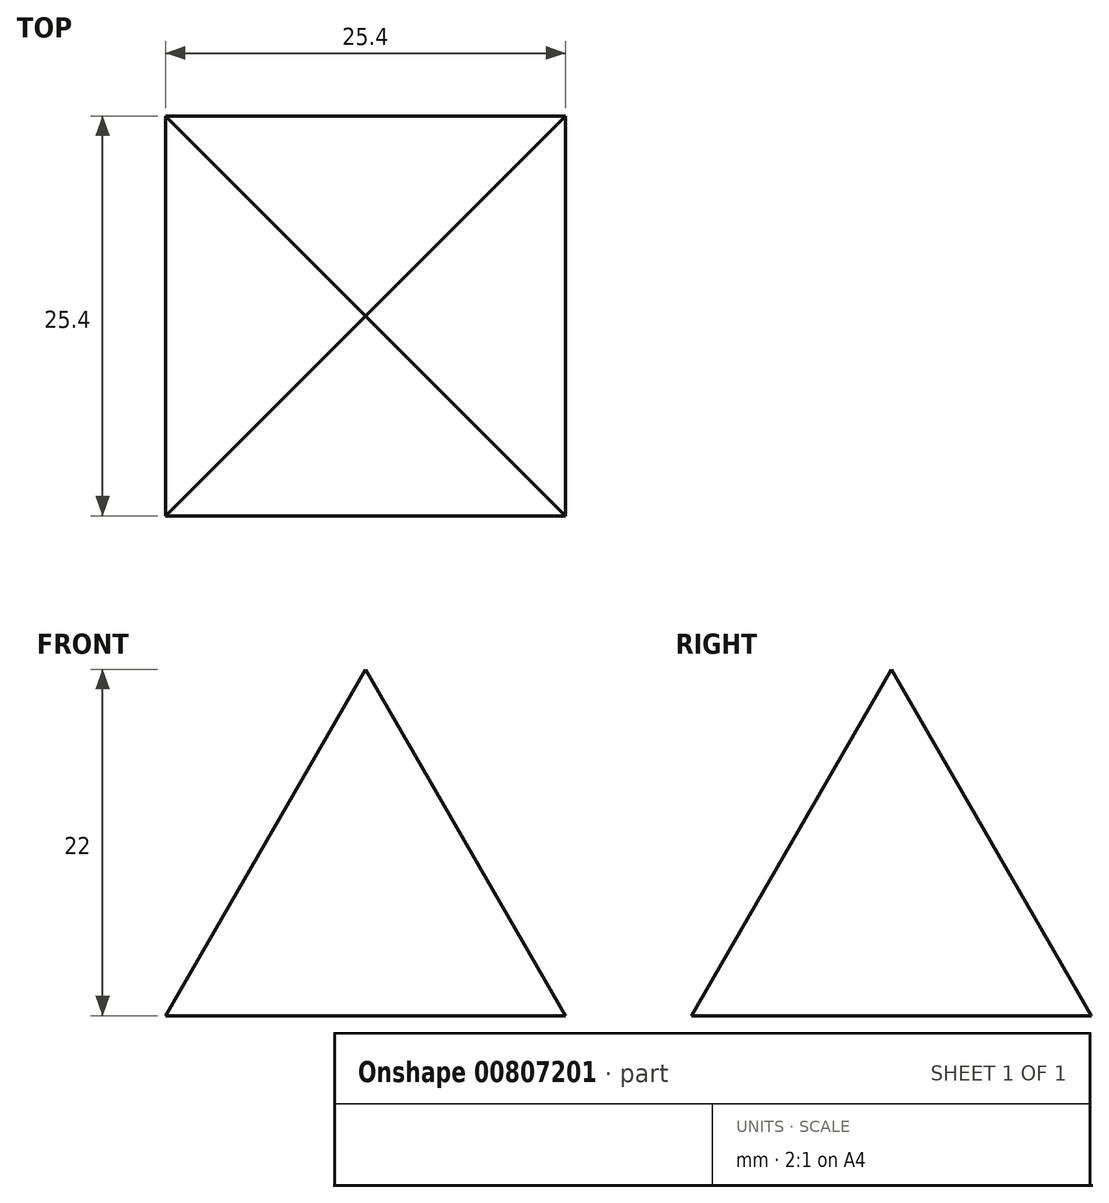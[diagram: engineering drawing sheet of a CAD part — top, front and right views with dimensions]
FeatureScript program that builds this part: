
annotation { "Feature Type Name" : "Feature", "Feature Type Description" : "" }
export const myFeature = defineFeature(function(context is Context, id is Id, definition is map)
    precondition{}
    {
        {
            var Q0;
            Q0=qCreatedBy(makeId("Top.planeOp"),FACE);
            var sketch = newSketch(context, id + "F0", { "sketchPlane" : qUnion([Q0])});
            skLineSegment(sketch, "E0.bottom", {"start": v(-31.21, 39.36) * mm, "end": v(-5.81, 39.36) * mm});
            skLineSegment(sketch, "E0.top", {"start": v(-31.21, 64.76) * mm, "end": v(-5.81, 64.76) * mm});
            skLineSegment(sketch, "E0.left", {"start": v(-31.21, 39.36) * mm, "end": v(-31.21, 64.76) * mm});
            skLineSegment(sketch, "E0.right", {"start": v(-5.81, 39.36) * mm, "end": v(-5.81, 64.76) * mm});
            skLineSegment(sketch, "E1.bottom", {"start": v(6.35, 39.36) * mm, "end": v(23.27, 39.36) * mm});
            skLineSegment(sketch, "E1.top", {"start": v(6.35, 25.45) * mm, "end": v(23.27, 25.45) * mm});
            skLineSegment(sketch, "E1.left", {"start": v(6.35, 39.36) * mm, "end": v(6.35, 25.45) * mm});
            skLineSegment(sketch, "E1.right", {"start": v(23.27, 39.36) * mm, "end": v(23.27, 25.45) * mm});
            skSolve(sketch);
        }
        {
            var Q0;
            Q0=makeQuery(id+"F0.imprint","IMPRINT",FACE,{"disambiguationData":[TD([[makeQuery(id+"F0.imprint","IMPRINT",EDGE,{"derivedFrom":sQuery(id+"F0.wireOp",EDGE,"E0.bottom")}),1.0]])]});
            extrude(context, id + "F1", {"entities" : qUnion([Q0]), "depth" : 37.6 * mm, "offsetDistance" : 25.4 * mm, "hasDraft" : true, "draftAngle" : 30 * degree, "draftPullDirection" : true});
        }
    });
